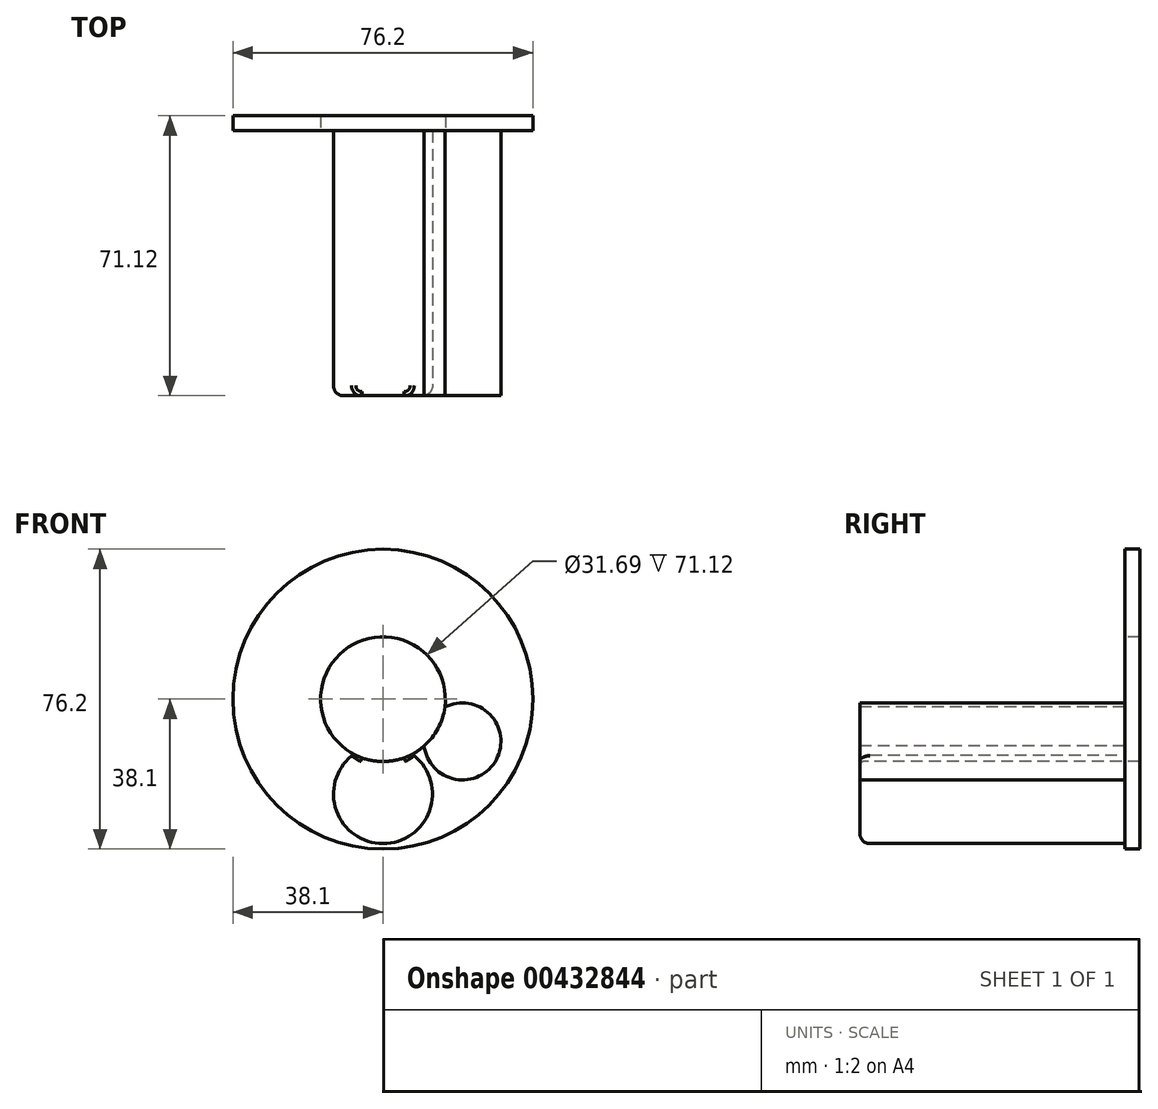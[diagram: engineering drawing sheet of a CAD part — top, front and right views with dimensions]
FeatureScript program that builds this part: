
annotation { "Feature Type Name" : "Feature", "Feature Type Description" : "" }
export const myFeature = defineFeature(function(context is Context, id is Id, definition is map)
    precondition{}
    {
        {
            var Q0;
            Q0=qCreatedBy(makeId("Front.planeOp"),FACE);
            var sketch = newSketch(context, id + "F0", { "sketchPlane" : qUnion([Q0])});
            skCircle(sketch, "E0", {"center": v(0, 0) * mm, "radius": 38.1 * mm});
            skSolve(sketch);
        }
        {
            var Q0;
            Q0=makeQuery(id+"F0.imprint","IMPRINT",FACE,{"disambiguationData":[TD([[makeQuery(id+"F0.imprint","IMPRINT",EDGE,{"derivedFrom":sQuery(id+"F0.wireOp",EDGE,"E0")}),1.0]])]});
            extrude(context, id + "F1", {"entities" : qUnion([Q0]), "depth" : 71.12 * mm});
        }
        {
            var Q0;
            Q0=makeQuery(id+"F1.opExtrude","CAP_FACE",FACE,{"disambiguationData":[OSD([sQuery(id+"F0.wireOp",EDGE,"E0")])],"isStart":false});
            var sketch = newSketch(context, id + "F2", { "sketchPlane" : qUnion([Q0])});
            skCircle(sketch, "E1", {"center": v(0, 24.13) * mm, "radius": 12.57 * mm});
            skCircle(sketch, "E2.MirrorC", {"center": v(0, -24.13) * mm, "radius": 12.57 * mm});
            skLineSegment(sketch, "E3", {"start": v(0, 0) * mm, "end": v(-44.2, 26.56) * mm});
            skCircle(sketch, "E4", {"center": v(-19.6, 11.77) * mm, "radius": 9.27 * mm});
            skCircle(sketch, "E5", {"center": v(20.18, 10.73) * mm, "radius": 9.78 * mm});
            skCircle(sketch, "E6.MirrorC", {"center": v(20.18, -10.73) * mm, "radius": 9.78 * mm});
            skCircle(sketch, "E7", {"center": v(-20.72, -9.66) * mm, "radius": 10.92 * mm});
            skLineSegment(sketch, "E8", {"start": v(0, 0) * mm, "end": v(-20.72, -9.66) * mm});
            skLineSegment(sketch, "E9", {"start": v(0, 0) * mm, "end": v(20.18, 10.73) * mm});
            skLineSegment(sketch, "E10", {"start": v(20.18, -10.73) * mm, "end": v(0, 0) * mm});
            skSolve(sketch);
        }
        {
            var Q0;
            {var subQ0=sQuery(id+"F2.wireOp",EDGE,"E4");var subQ1=sQuery(id+"F2.wireOp",EDGE,"E3");var subQ2=makeQuery(id+"F2.imprint","INTERSECT",VERTEX,{"disambiguationData":[OD(0.0)],"derivedFrom":[subQ1,subQ0]});Q0=makeQuery(id+"F2.imprint","IMPRINT",FACE,{"disambiguationData":[TD([[makeQuery(id+"F2.imprint","IMPRINT",EDGE,{"disambiguationData":[TD([[subQ2,1.0]])],"derivedFrom":subQ1}),-1.0]])]});}
            var Q1;
            {var subQ0=sQuery(id+"F2.wireOp",EDGE,"E4");var subQ1=sQuery(id+"F2.wireOp",EDGE,"E3");var subQ2=makeQuery(id+"F2.imprint","INTERSECT",VERTEX,{"disambiguationData":[OD(0.0)],"derivedFrom":[subQ1,subQ0]});Q1=makeQuery(id+"F2.imprint","IMPRINT",FACE,{"disambiguationData":[TD([[makeQuery(id+"F2.imprint","IMPRINT",EDGE,{"disambiguationData":[TD([[subQ2,1.0]])],"derivedFrom":subQ1}),1.0]])]});}
            var Q2;
            Q2=makeQuery(id+"F2.imprint","IMPRINT",FACE,{"disambiguationData":[TD([[makeQuery(id+"F2.imprint","IMPRINT",EDGE,{"derivedFrom":sQuery(id+"F2.wireOp",EDGE,"E1")}),1.0]])]});
            var Q3;
            Q3=makeQuery(id+"F2.imprint","IMPRINT",FACE,{"disambiguationData":[TD([[makeQuery(id+"F2.imprint","IMPRINT",EDGE,{"derivedFrom":sQuery(id+"F2.wireOp",EDGE,"E5")}),1.0]])]});
            var Q4;
            Q4=makeQuery(id+"F2.imprint","IMPRINT",FACE,{"disambiguationData":[TD([[makeQuery(id+"F2.imprint","IMPRINT",EDGE,{"derivedFrom":sQuery(id+"F2.wireOp",EDGE,"E6.MirrorC")}),-1.0]])]});
            var Q5;
            Q5=makeQuery(id+"F2.imprint","IMPRINT",FACE,{"disambiguationData":[TD([[makeQuery(id+"F2.imprint","IMPRINT",EDGE,{"derivedFrom":sQuery(id+"F2.wireOp",EDGE,"E2.MirrorC")}),-1.0]])]});
            var Q6;
            Q6=makeQuery(id+"F2.imprint","IMPRINT",FACE,{"disambiguationData":[TD([[makeQuery(id+"F2.imprint","IMPRINT",EDGE,{"derivedFrom":sQuery(id+"F2.wireOp",EDGE,"E7")}),1.0]])]});
            extrude(context, id + "F3", {"entities" : qUnion([Q0, Q1, Q2, Q3, Q4, Q5, Q6]), "operationType" : NewBodyOperationType.REMOVE, "oppositeDirection" : true, "depth" : 67.3 * mm});
        }
        {
            var Q0;
            Q0=makeQuery(id+"F1.opExtrude","CAP_FACE",FACE,{"disambiguationData":[OSD([sQuery(id+"F0.wireOp",EDGE,"E0")])],"isStart":false});
            var sketch = newSketch(context, id + "F4", { "sketchPlane" : qUnion([Q0])});
            skCircle(sketch, "E11", {"center": v(0, 0) * mm, "radius": 15.84 * mm});
            skSolve(sketch);
        }
        {
            var Q0;
            {var subQ0=sQuery(id+"F4.wireOp",EDGE,"E11");var subQ1=makeQuery(id+"F3.boolean.opBoolean","COPY",EDGE,{"derivedFrom":makeQuery(id+"F3.opExtrude","CAP_EDGE",EDGE,{"disambiguationData":[OSD([sQuery(id+"F2.wireOp",EDGE,"E1")])],"isStart":true})});var subQ2=makeQuery(id+"F4.imprint","INTERSECT",VERTEX,{"disambiguationData":[OD(0.0)],"derivedFrom":[subQ1,subQ0]});Q0=makeQuery(id+"F4.imprint","IMPRINT",FACE,{"disambiguationData":[TD([[makeQuery(id+"F4.imprint","IMPRINT",EDGE,{"disambiguationData":[TD([[subQ2,-1.0]])],"derivedFrom":subQ0}),1.0]])]});}
            var Q1;
            {var subQ0=sQuery(id+"F4.wireOp",EDGE,"E11");var subQ1=makeQuery(id+"F3.boolean.opBoolean","COPY",EDGE,{"derivedFrom":makeQuery(id+"F3.opExtrude","CAP_EDGE",EDGE,{"disambiguationData":[OSD([sQuery(id+"F2.wireOp",EDGE,"E1")])],"isStart":true})});var subQ2=makeQuery(id+"F4.imprint","INTERSECT",VERTEX,{"disambiguationData":[OD(0.0)],"derivedFrom":[subQ1,subQ0]});Q1=makeQuery(id+"F4.imprint","IMPRINT",FACE,{"disambiguationData":[TD([[makeQuery(id+"F4.imprint","IMPRINT",EDGE,{"disambiguationData":[TD([[subQ2,1.0]])],"derivedFrom":subQ0}),1.0]])]});}
            var Q2;
            {var subQ0=sQuery(id+"F4.wireOp",EDGE,"E11");var subQ1=makeQuery(id+"F3.boolean.opBoolean","COPY",EDGE,{"derivedFrom":makeQuery(id+"F3.opExtrude","CAP_EDGE",EDGE,{"disambiguationData":[OSD([sQuery(id+"F2.wireOp",EDGE,"E2.MirrorC")])],"isStart":true})});var subQ2=makeQuery(id+"F4.imprint","INTERSECT",VERTEX,{"disambiguationData":[OD(0.0)],"derivedFrom":[subQ1,subQ0]});Q2=makeQuery(id+"F4.imprint","IMPRINT",FACE,{"disambiguationData":[TD([[makeQuery(id+"F4.imprint","IMPRINT",EDGE,{"disambiguationData":[TD([[subQ2,-1.0]])],"derivedFrom":subQ0}),1.0]])]});}
            var Q3;
            {var subQ0=sQuery(id+"F4.wireOp",EDGE,"E11");var subQ1=makeQuery(id+"F3.boolean.opBoolean","COPY",EDGE,{"derivedFrom":makeQuery(id+"F3.opExtrude","CAP_EDGE",EDGE,{"disambiguationData":[OSD([sQuery(id+"F2.wireOp",EDGE,"E7")])],"isStart":true})});var subQ2=makeQuery(id+"F4.imprint","INTERSECT",VERTEX,{"disambiguationData":[OD(0.0)],"derivedFrom":[subQ1,subQ0]});Q3=makeQuery(id+"F4.imprint","IMPRINT",FACE,{"disambiguationData":[TD([[makeQuery(id+"F4.imprint","IMPRINT",EDGE,{"disambiguationData":[TD([[subQ2,-1.0]])],"derivedFrom":subQ0}),1.0]])]});}
            var Q4;
            {var subQ0=sQuery(id+"F4.wireOp",EDGE,"E11");var subQ1=makeQuery(id+"F3.boolean.opBoolean","COPY",EDGE,{"derivedFrom":makeQuery(id+"F3.opExtrude","CAP_EDGE",EDGE,{"disambiguationData":[OSD([sQuery(id+"F2.wireOp",EDGE,"E5")])],"isStart":true})});var subQ2=makeQuery(id+"F4.imprint","INTERSECT",VERTEX,{"disambiguationData":[OD(0.0)],"derivedFrom":[subQ1,subQ0]});Q4=makeQuery(id+"F4.imprint","IMPRINT",FACE,{"disambiguationData":[TD([[makeQuery(id+"F4.imprint","IMPRINT",EDGE,{"disambiguationData":[TD([[subQ2,1.0]])],"derivedFrom":subQ0}),1.0]])]});}
            var Q5;
            {var subQ0=sQuery(id+"F4.wireOp",EDGE,"E11");var subQ1=makeQuery(id+"F3.boolean.opBoolean","COPY",EDGE,{"derivedFrom":makeQuery(id+"F3.opExtrude","CAP_EDGE",EDGE,{"disambiguationData":[OSD([sQuery(id+"F2.wireOp",EDGE,"E6.MirrorC")])],"isStart":true})});var subQ2=makeQuery(id+"F4.imprint","INTERSECT",VERTEX,{"disambiguationData":[OD(0.0)],"derivedFrom":[subQ1,subQ0]});Q5=makeQuery(id+"F4.imprint","IMPRINT",FACE,{"disambiguationData":[TD([[makeQuery(id+"F4.imprint","IMPRINT",EDGE,{"disambiguationData":[TD([[subQ2,-1.0]])],"derivedFrom":subQ0}),1.0]])]});}
            var Q6;
            {var subQ0=sQuery(id+"F4.wireOp",EDGE,"E11");var subQ1=makeQuery(id+"F3.boolean.opBoolean","COPY",EDGE,{"derivedFrom":makeQuery(id+"F3.opExtrude","CAP_EDGE",EDGE,{"disambiguationData":[OSD([sQuery(id+"F2.wireOp",EDGE,"E4")])],"isStart":true})});var subQ2=makeQuery(id+"F4.imprint","INTERSECT",VERTEX,{"disambiguationData":[OD(0.0)],"derivedFrom":[subQ1,subQ0]});Q6=makeQuery(id+"F4.imprint","IMPRINT",FACE,{"disambiguationData":[TD([[makeQuery(id+"F4.imprint","IMPRINT",EDGE,{"disambiguationData":[TD([[subQ2,-1.0]])],"derivedFrom":subQ0}),1.0]])]});}
            extrude(context, id + "F5", {"entities" : qUnion([Q0, Q1, Q2, Q3, Q4, Q5, Q6]), "operationType" : NewBodyOperationType.REMOVE, "oppositeDirection" : true, "depth" : 85.1 * mm});
        }
        {
            var Q0;
            Q0=makeQuery(id+"F3.boolean.opBoolean","COPY",EDGE,{"derivedFrom":makeQuery(id+"F3.opExtrude","CAP_EDGE",EDGE,{"disambiguationData":[OSD([sQuery(id+"F2.wireOp",EDGE,"E4")])],"isStart":true})});
            var Q1;
            Q1=makeQuery(id+"F3.boolean.opBoolean","COPY",EDGE,{"derivedFrom":makeQuery(id+"F3.opExtrude","CAP_EDGE",EDGE,{"disambiguationData":[OSD([sQuery(id+"F2.wireOp",EDGE,"E1")])],"isStart":true})});
            var Q2;
            Q2=makeQuery(id+"F3.boolean.opBoolean","COPY",EDGE,{"derivedFrom":makeQuery(id+"F3.opExtrude","CAP_EDGE",EDGE,{"disambiguationData":[OSD([sQuery(id+"F2.wireOp",EDGE,"E7")])],"isStart":true})});
            var Q3;
            Q3=makeQuery(id+"F3.boolean.opBoolean","COPY",EDGE,{"derivedFrom":makeQuery(id+"F3.opExtrude","CAP_EDGE",EDGE,{"disambiguationData":[OSD([sQuery(id+"F2.wireOp",EDGE,"E2.MirrorC")])],"isStart":true})});
            var Q4;
            Q4=makeQuery(id+"F3.boolean.opBoolean","COPY",EDGE,{"derivedFrom":makeQuery(id+"F3.opExtrude","CAP_EDGE",EDGE,{"disambiguationData":[OSD([sQuery(id+"F2.wireOp",EDGE,"E6.MirrorC")])],"isStart":true})});
            var Q5;
            Q5=makeQuery(id+"F3.boolean.opBoolean","COPY",EDGE,{"derivedFrom":makeQuery(id+"F3.opExtrude","CAP_EDGE",EDGE,{"disambiguationData":[OSD([sQuery(id+"F2.wireOp",EDGE,"E5")])],"isStart":true})});
            var Q6;
            Q6=makeQuery(id+"F1.opExtrude","CAP_EDGE",EDGE,{"disambiguationData":[OSD([sQuery(id+"F0.wireOp",EDGE,"E0")])],"isStart":false});
            fillet(context, id + "F6", {"entities" : qUnion([Q0, Q1, Q2, Q3, Q4, Q5, Q6]), "radius" : 2.54 * mm, "tangentPropagation" : true, "allowEdgeOverflow" : false});
        }
        {
            var Q0;
            {var subQ0=sQuery(id+"F4.wireOp",EDGE,"E11");var subQ1=sQuery(id+"F2.wireOp",EDGE,"E1");var subQ2=makeQuery(id+"F3.boolean.opBoolean","COPY",EDGE,{"derivedFrom":makeQuery(id+"F3.opExtrude","CAP_EDGE",EDGE,{"disambiguationData":[OSD([subQ1])],"isStart":true})});var subQ3=makeQuery(id+"F4.imprint","INTERSECT",VERTEX,{"disambiguationData":[OD(1.0)],"derivedFrom":[subQ2,subQ0]});var subQ4=makeQuery(id+"F4.imprint","INTERSECT",VERTEX,{"disambiguationData":[OD(0.0)],"derivedFrom":[subQ2,subQ0]});Q0=makeQuery(id+"F5.boolean.opBoolean","INTERSECT",EDGE,{"disambiguationData":[OD(0.0)],"derivedFrom":[makeQuery(id+"F3.boolean.opBoolean","COPY",FACE,{"derivedFrom":makeQuery(id+"F3.opExtrude","SWEPT_FACE",FACE,{"disambiguationData":[OSD([subQ1])]})}),makeQuery(id+"F5.opExtrude","SWEPT_FACE",FACE,{"disambiguationData":[OSD([subQ0]),TDD([makeQuery(id+"F4.imprint","IMPRINT",EDGE,{"disambiguationData":[TD([[makeQuery(id+"F4.imprint","INTERSECT",VERTEX,{"disambiguationData":[OD(0.0)],"derivedFrom":[makeQuery(id+"F3.boolean.opBoolean","COPY",EDGE,{"derivedFrom":makeQuery(id+"F3.opExtrude","CAP_EDGE",EDGE,{"disambiguationData":[OSD([sQuery(id+"F2.wireOp",EDGE,"E5")])],"isStart":true})}),subQ0]}),-1.0]])],"derivedFrom":subQ0}),makeQuery(id+"F4.imprint","IMPRINT",EDGE,{"disambiguationData":[TD([[subQ4,-1.0]])],"derivedFrom":subQ0}),makeQuery(id+"F4.imprint","IMPRINT",EDGE,{"disambiguationData":[TD([[subQ3,-1.0]])],"derivedFrom":subQ0})])]})]});}
            var Q1;
            {var subQ0=sQuery(id+"F2.wireOp",EDGE,"E5");var subQ1=sQuery(id+"F4.wireOp",EDGE,"E11");var subQ5=makeQuery(id+"F4.imprint","INTERSECT",VERTEX,{"disambiguationData":[OD(0.0)],"derivedFrom":[makeQuery(id+"F3.boolean.opBoolean","COPY",EDGE,{"derivedFrom":makeQuery(id+"F3.opExtrude","CAP_EDGE",EDGE,{"disambiguationData":[OSD([subQ0])],"isStart":true})}),subQ1]});Q1=makeQuery(id+"F5.boolean.opBoolean","COPY",EDGE,{"disambiguationData":[topologyDisambiguationEdgeConnected([makeQuery(id+"F3.boolean.opBoolean","COPY",FACE,{"derivedFrom":makeQuery(id+"F3.opExtrude","SWEPT_FACE",FACE,{"disambiguationData":[OSD([subQ0])]})})])],"derivedFrom":makeQuery(id+"F5.opExtrude","SWEPT_EDGE",EDGE,{"disambiguationData":[OSD([subQ0,subQ1]),TDD([subQ5])]})});}
            var Q2;
            {var subQ0=sQuery(id+"F4.wireOp",EDGE,"E11");var subQ1=sQuery(id+"F2.wireOp",EDGE,"E1");var subQ2=makeQuery(id+"F3.boolean.opBoolean","COPY",EDGE,{"derivedFrom":makeQuery(id+"F3.opExtrude","CAP_EDGE",EDGE,{"disambiguationData":[OSD([subQ1])],"isStart":true})});var subQ3=makeQuery(id+"F4.imprint","INTERSECT",VERTEX,{"disambiguationData":[OD(1.0)],"derivedFrom":[subQ2,subQ0]});var subQ4=makeQuery(id+"F4.imprint","INTERSECT",VERTEX,{"disambiguationData":[OD(0.0)],"derivedFrom":[subQ2,subQ0]});Q2=makeQuery(id+"F5.boolean.opBoolean","INTERSECT",EDGE,{"disambiguationData":[OD(1.0)],"derivedFrom":[makeQuery(id+"F3.boolean.opBoolean","COPY",FACE,{"derivedFrom":makeQuery(id+"F3.opExtrude","SWEPT_FACE",FACE,{"disambiguationData":[OSD([subQ1])]})}),makeQuery(id+"F5.opExtrude","SWEPT_FACE",FACE,{"disambiguationData":[OSD([subQ0]),TDD([makeQuery(id+"F4.imprint","IMPRINT",EDGE,{"disambiguationData":[TD([[makeQuery(id+"F4.imprint","INTERSECT",VERTEX,{"disambiguationData":[OD(0.0)],"derivedFrom":[makeQuery(id+"F3.boolean.opBoolean","COPY",EDGE,{"derivedFrom":makeQuery(id+"F3.opExtrude","CAP_EDGE",EDGE,{"disambiguationData":[OSD([sQuery(id+"F2.wireOp",EDGE,"E5")])],"isStart":true})}),subQ0]}),-1.0]])],"derivedFrom":subQ0}),makeQuery(id+"F4.imprint","IMPRINT",EDGE,{"disambiguationData":[TD([[subQ4,-1.0]])],"derivedFrom":subQ0}),makeQuery(id+"F4.imprint","IMPRINT",EDGE,{"disambiguationData":[TD([[subQ3,-1.0]])],"derivedFrom":subQ0})])]})]});}
            var Q3;
            {var subQ0=sQuery(id+"F2.wireOp",EDGE,"E5");var subQ1=sQuery(id+"F4.wireOp",EDGE,"E11");var subQ2=makeQuery(id+"F4.imprint","INTERSECT",VERTEX,{"disambiguationData":[OD(1.0)],"derivedFrom":[makeQuery(id+"F3.boolean.opBoolean","COPY",EDGE,{"derivedFrom":makeQuery(id+"F3.opExtrude","CAP_EDGE",EDGE,{"disambiguationData":[OSD([subQ0])],"isStart":true})}),subQ1]});Q3=makeQuery(id+"F5.boolean.opBoolean","COPY",EDGE,{"disambiguationData":[topologyDisambiguationEdgeConnected([makeQuery(id+"F3.boolean.opBoolean","COPY",FACE,{"derivedFrom":makeQuery(id+"F3.opExtrude","SWEPT_FACE",FACE,{"disambiguationData":[OSD([subQ0])]})})])],"derivedFrom":makeQuery(id+"F5.opExtrude","SWEPT_EDGE",EDGE,{"disambiguationData":[OSD([subQ0,subQ1]),TDD([subQ2])]})});}
            var Q4;
            {var subQ0=sQuery(id+"F2.wireOp",EDGE,"E6.MirrorC");var subQ1=sQuery(id+"F4.wireOp",EDGE,"E11");var subQ2=makeQuery(id+"F4.imprint","INTERSECT",VERTEX,{"disambiguationData":[OD(1.0)],"derivedFrom":[makeQuery(id+"F3.boolean.opBoolean","COPY",EDGE,{"derivedFrom":makeQuery(id+"F3.opExtrude","CAP_EDGE",EDGE,{"disambiguationData":[OSD([subQ0])],"isStart":true})}),subQ1]});Q4=makeQuery(id+"F5.boolean.opBoolean","COPY",EDGE,{"disambiguationData":[topologyDisambiguationEdgeConnected([makeQuery(id+"F3.boolean.opBoolean","COPY",FACE,{"derivedFrom":makeQuery(id+"F3.opExtrude","SWEPT_FACE",FACE,{"disambiguationData":[OSD([subQ0])]})})])],"derivedFrom":makeQuery(id+"F5.opExtrude","SWEPT_EDGE",EDGE,{"disambiguationData":[OSD([subQ0,subQ1]),TDD([subQ2])]})});}
            var Q5;
            {var subQ0=sQuery(id+"F2.wireOp",EDGE,"E6.MirrorC");var subQ1=sQuery(id+"F4.wireOp",EDGE,"E11");var subQ4=makeQuery(id+"F4.imprint","INTERSECT",VERTEX,{"disambiguationData":[OD(0.0)],"derivedFrom":[makeQuery(id+"F3.boolean.opBoolean","COPY",EDGE,{"derivedFrom":makeQuery(id+"F3.opExtrude","CAP_EDGE",EDGE,{"disambiguationData":[OSD([subQ0])],"isStart":true})}),subQ1]});Q5=makeQuery(id+"F5.boolean.opBoolean","COPY",EDGE,{"disambiguationData":[topologyDisambiguationEdgeConnected([makeQuery(id+"F3.boolean.opBoolean","COPY",FACE,{"derivedFrom":makeQuery(id+"F3.opExtrude","SWEPT_FACE",FACE,{"disambiguationData":[OSD([subQ0])]})})])],"derivedFrom":makeQuery(id+"F5.opExtrude","SWEPT_EDGE",EDGE,{"disambiguationData":[OSD([subQ0,subQ1]),TDD([subQ4])]})});}
            var Q6;
            {var subQ0=sQuery(id+"F4.wireOp",EDGE,"E11");var subQ1=sQuery(id+"F2.wireOp",EDGE,"E2.MirrorC");var subQ2=makeQuery(id+"F3.boolean.opBoolean","COPY",EDGE,{"derivedFrom":makeQuery(id+"F3.opExtrude","CAP_EDGE",EDGE,{"disambiguationData":[OSD([subQ1])],"isStart":true})});var subQ3=makeQuery(id+"F4.imprint","INTERSECT",VERTEX,{"disambiguationData":[OD(1.0)],"derivedFrom":[subQ2,subQ0]});var subQ4=makeQuery(id+"F4.imprint","INTERSECT",VERTEX,{"disambiguationData":[OD(0.0)],"derivedFrom":[subQ2,subQ0]});var subQ5=makeQuery(id+"F3.boolean.opBoolean","COPY",EDGE,{"derivedFrom":makeQuery(id+"F3.opExtrude","CAP_EDGE",EDGE,{"disambiguationData":[OSD([sQuery(id+"F2.wireOp",EDGE,"E7")])],"isStart":true})});var subQ6=makeQuery(id+"F4.imprint","INTERSECT",VERTEX,{"disambiguationData":[OD(1.0)],"derivedFrom":[subQ5,subQ0]});var subQ7=makeQuery(id+"F4.imprint","INTERSECT",VERTEX,{"disambiguationData":[OD(0.0)],"derivedFrom":[subQ5,subQ0]});Q6=makeQuery(id+"F5.boolean.opBoolean","INTERSECT",EDGE,{"disambiguationData":[OD(0.0)],"derivedFrom":[makeQuery(id+"F3.boolean.opBoolean","COPY",FACE,{"derivedFrom":makeQuery(id+"F3.opExtrude","SWEPT_FACE",FACE,{"disambiguationData":[OSD([subQ1])]})}),makeQuery(id+"F5.opExtrude","SWEPT_FACE",FACE,{"disambiguationData":[OSD([subQ0]),TDD([makeQuery(id+"F4.imprint","IMPRINT",EDGE,{"disambiguationData":[TD([[makeQuery(id+"F4.imprint","INTERSECT",VERTEX,{"disambiguationData":[OD(1.0)],"derivedFrom":[makeQuery(id+"F3.boolean.opBoolean","COPY",EDGE,{"derivedFrom":makeQuery(id+"F3.opExtrude","CAP_EDGE",EDGE,{"disambiguationData":[OSD([sQuery(id+"F2.wireOp",EDGE,"E4")])],"isStart":true})}),subQ0]}),-1.0]])],"derivedFrom":subQ0}),makeQuery(id+"F4.imprint","IMPRINT",EDGE,{"disambiguationData":[TD([[subQ7,-1.0]])],"derivedFrom":subQ0}),makeQuery(id+"F4.imprint","IMPRINT",EDGE,{"disambiguationData":[TD([[subQ6,-1.0]])],"derivedFrom":subQ0}),makeQuery(id+"F4.imprint","IMPRINT",EDGE,{"disambiguationData":[TD([[subQ4,-1.0]])],"derivedFrom":subQ0}),makeQuery(id+"F4.imprint","IMPRINT",EDGE,{"disambiguationData":[TD([[subQ3,-1.0]])],"derivedFrom":subQ0})])]})]});}
            var Q7;
            {var subQ0=sQuery(id+"F4.wireOp",EDGE,"E11");var subQ1=sQuery(id+"F2.wireOp",EDGE,"E2.MirrorC");var subQ2=makeQuery(id+"F3.boolean.opBoolean","COPY",EDGE,{"derivedFrom":makeQuery(id+"F3.opExtrude","CAP_EDGE",EDGE,{"disambiguationData":[OSD([subQ1])],"isStart":true})});var subQ3=makeQuery(id+"F4.imprint","INTERSECT",VERTEX,{"disambiguationData":[OD(1.0)],"derivedFrom":[subQ2,subQ0]});var subQ4=makeQuery(id+"F4.imprint","INTERSECT",VERTEX,{"disambiguationData":[OD(0.0)],"derivedFrom":[subQ2,subQ0]});var subQ5=makeQuery(id+"F3.boolean.opBoolean","COPY",EDGE,{"derivedFrom":makeQuery(id+"F3.opExtrude","CAP_EDGE",EDGE,{"disambiguationData":[OSD([sQuery(id+"F2.wireOp",EDGE,"E7")])],"isStart":true})});var subQ6=makeQuery(id+"F4.imprint","INTERSECT",VERTEX,{"disambiguationData":[OD(1.0)],"derivedFrom":[subQ5,subQ0]});var subQ7=makeQuery(id+"F4.imprint","INTERSECT",VERTEX,{"disambiguationData":[OD(0.0)],"derivedFrom":[subQ5,subQ0]});Q7=makeQuery(id+"F5.boolean.opBoolean","INTERSECT",EDGE,{"disambiguationData":[OD(1.0)],"derivedFrom":[makeQuery(id+"F3.boolean.opBoolean","COPY",FACE,{"derivedFrom":makeQuery(id+"F3.opExtrude","SWEPT_FACE",FACE,{"disambiguationData":[OSD([subQ1])]})}),makeQuery(id+"F5.opExtrude","SWEPT_FACE",FACE,{"disambiguationData":[OSD([subQ0]),TDD([makeQuery(id+"F4.imprint","IMPRINT",EDGE,{"disambiguationData":[TD([[makeQuery(id+"F4.imprint","INTERSECT",VERTEX,{"disambiguationData":[OD(1.0)],"derivedFrom":[makeQuery(id+"F3.boolean.opBoolean","COPY",EDGE,{"derivedFrom":makeQuery(id+"F3.opExtrude","CAP_EDGE",EDGE,{"disambiguationData":[OSD([sQuery(id+"F2.wireOp",EDGE,"E4")])],"isStart":true})}),subQ0]}),-1.0]])],"derivedFrom":subQ0}),makeQuery(id+"F4.imprint","IMPRINT",EDGE,{"disambiguationData":[TD([[subQ7,-1.0]])],"derivedFrom":subQ0}),makeQuery(id+"F4.imprint","IMPRINT",EDGE,{"disambiguationData":[TD([[subQ6,-1.0]])],"derivedFrom":subQ0}),makeQuery(id+"F4.imprint","IMPRINT",EDGE,{"disambiguationData":[TD([[subQ4,-1.0]])],"derivedFrom":subQ0}),makeQuery(id+"F4.imprint","IMPRINT",EDGE,{"disambiguationData":[TD([[subQ3,-1.0]])],"derivedFrom":subQ0})])]})]});}
            var Q8;
            {var subQ0=sQuery(id+"F2.wireOp",EDGE,"E4");var subQ1=sQuery(id+"F4.wireOp",EDGE,"E11");var subQ8=makeQuery(id+"F4.imprint","INTERSECT",VERTEX,{"disambiguationData":[OD(1.0)],"derivedFrom":[makeQuery(id+"F3.boolean.opBoolean","COPY",EDGE,{"derivedFrom":makeQuery(id+"F3.opExtrude","CAP_EDGE",EDGE,{"disambiguationData":[OSD([subQ0])],"isStart":true})}),subQ1]});Q8=makeQuery(id+"F5.boolean.opBoolean","COPY",EDGE,{"disambiguationData":[topologyDisambiguationEdgeConnected([makeQuery(id+"F3.boolean.opBoolean","COPY",FACE,{"derivedFrom":makeQuery(id+"F3.opExtrude","SWEPT_FACE",FACE,{"disambiguationData":[OSD([subQ0])]})})])],"derivedFrom":makeQuery(id+"F5.opExtrude","SWEPT_EDGE",EDGE,{"disambiguationData":[OSD([subQ0,subQ1]),TDD([subQ8])]})});}
            var Q9;
            {var subQ0=sQuery(id+"F4.wireOp",EDGE,"E11");var subQ1=makeQuery(id+"F3.boolean.opBoolean","COPY",EDGE,{"derivedFrom":makeQuery(id+"F3.opExtrude","CAP_EDGE",EDGE,{"disambiguationData":[OSD([sQuery(id+"F2.wireOp",EDGE,"E2.MirrorC")])],"isStart":true})});var subQ2=makeQuery(id+"F4.imprint","INTERSECT",VERTEX,{"disambiguationData":[OD(1.0)],"derivedFrom":[subQ1,subQ0]});var subQ3=makeQuery(id+"F4.imprint","INTERSECT",VERTEX,{"disambiguationData":[OD(0.0)],"derivedFrom":[subQ1,subQ0]});var subQ4=sQuery(id+"F2.wireOp",EDGE,"E7");var subQ5=makeQuery(id+"F3.boolean.opBoolean","COPY",EDGE,{"derivedFrom":makeQuery(id+"F3.opExtrude","CAP_EDGE",EDGE,{"disambiguationData":[OSD([subQ4])],"isStart":true})});var subQ6=makeQuery(id+"F4.imprint","INTERSECT",VERTEX,{"disambiguationData":[OD(1.0)],"derivedFrom":[subQ5,subQ0]});var subQ7=makeQuery(id+"F4.imprint","INTERSECT",VERTEX,{"disambiguationData":[OD(0.0)],"derivedFrom":[subQ5,subQ0]});Q9=makeQuery(id+"F5.boolean.opBoolean","INTERSECT",EDGE,{"disambiguationData":[OD(0.0)],"derivedFrom":[makeQuery(id+"F3.boolean.opBoolean","COPY",FACE,{"derivedFrom":makeQuery(id+"F3.opExtrude","SWEPT_FACE",FACE,{"disambiguationData":[OSD([subQ4])]})}),makeQuery(id+"F5.opExtrude","SWEPT_FACE",FACE,{"disambiguationData":[OSD([subQ0]),TDD([makeQuery(id+"F4.imprint","IMPRINT",EDGE,{"disambiguationData":[TD([[makeQuery(id+"F4.imprint","INTERSECT",VERTEX,{"disambiguationData":[OD(1.0)],"derivedFrom":[makeQuery(id+"F3.boolean.opBoolean","COPY",EDGE,{"derivedFrom":makeQuery(id+"F3.opExtrude","CAP_EDGE",EDGE,{"disambiguationData":[OSD([sQuery(id+"F2.wireOp",EDGE,"E4")])],"isStart":true})}),subQ0]}),-1.0]])],"derivedFrom":subQ0}),makeQuery(id+"F4.imprint","IMPRINT",EDGE,{"disambiguationData":[TD([[subQ7,-1.0]])],"derivedFrom":subQ0}),makeQuery(id+"F4.imprint","IMPRINT",EDGE,{"disambiguationData":[TD([[subQ6,-1.0]])],"derivedFrom":subQ0}),makeQuery(id+"F4.imprint","IMPRINT",EDGE,{"disambiguationData":[TD([[subQ3,-1.0]])],"derivedFrom":subQ0}),makeQuery(id+"F4.imprint","IMPRINT",EDGE,{"disambiguationData":[TD([[subQ2,-1.0]])],"derivedFrom":subQ0})])]})]});}
            var Q10;
            {var subQ0=sQuery(id+"F2.wireOp",EDGE,"E4");var subQ1=sQuery(id+"F4.wireOp",EDGE,"E11");var subQ4=makeQuery(id+"F4.imprint","INTERSECT",VERTEX,{"disambiguationData":[OD(0.0)],"derivedFrom":[makeQuery(id+"F3.boolean.opBoolean","COPY",EDGE,{"derivedFrom":makeQuery(id+"F3.opExtrude","CAP_EDGE",EDGE,{"disambiguationData":[OSD([subQ0])],"isStart":true})}),subQ1]});Q10=makeQuery(id+"F5.boolean.opBoolean","COPY",EDGE,{"disambiguationData":[topologyDisambiguationEdgeConnected([makeQuery(id+"F3.boolean.opBoolean","COPY",FACE,{"derivedFrom":makeQuery(id+"F3.opExtrude","SWEPT_FACE",FACE,{"disambiguationData":[OSD([subQ0])]})})])],"derivedFrom":makeQuery(id+"F5.opExtrude","SWEPT_EDGE",EDGE,{"disambiguationData":[OSD([subQ0,subQ1]),TDD([subQ4])]})});}
            var Q11;
            {var subQ0=sQuery(id+"F4.wireOp",EDGE,"E11");var subQ1=makeQuery(id+"F3.boolean.opBoolean","COPY",EDGE,{"derivedFrom":makeQuery(id+"F3.opExtrude","CAP_EDGE",EDGE,{"disambiguationData":[OSD([sQuery(id+"F2.wireOp",EDGE,"E2.MirrorC")])],"isStart":true})});var subQ2=makeQuery(id+"F4.imprint","INTERSECT",VERTEX,{"disambiguationData":[OD(1.0)],"derivedFrom":[subQ1,subQ0]});var subQ3=makeQuery(id+"F4.imprint","INTERSECT",VERTEX,{"disambiguationData":[OD(0.0)],"derivedFrom":[subQ1,subQ0]});var subQ4=sQuery(id+"F2.wireOp",EDGE,"E7");var subQ5=makeQuery(id+"F3.boolean.opBoolean","COPY",EDGE,{"derivedFrom":makeQuery(id+"F3.opExtrude","CAP_EDGE",EDGE,{"disambiguationData":[OSD([subQ4])],"isStart":true})});var subQ6=makeQuery(id+"F4.imprint","INTERSECT",VERTEX,{"disambiguationData":[OD(1.0)],"derivedFrom":[subQ5,subQ0]});var subQ7=makeQuery(id+"F4.imprint","INTERSECT",VERTEX,{"disambiguationData":[OD(0.0)],"derivedFrom":[subQ5,subQ0]});Q11=makeQuery(id+"F5.boolean.opBoolean","INTERSECT",EDGE,{"disambiguationData":[OD(1.0)],"derivedFrom":[makeQuery(id+"F3.boolean.opBoolean","COPY",FACE,{"derivedFrom":makeQuery(id+"F3.opExtrude","SWEPT_FACE",FACE,{"disambiguationData":[OSD([subQ4])]})}),makeQuery(id+"F5.opExtrude","SWEPT_FACE",FACE,{"disambiguationData":[OSD([subQ0]),TDD([makeQuery(id+"F4.imprint","IMPRINT",EDGE,{"disambiguationData":[TD([[makeQuery(id+"F4.imprint","INTERSECT",VERTEX,{"disambiguationData":[OD(1.0)],"derivedFrom":[makeQuery(id+"F3.boolean.opBoolean","COPY",EDGE,{"derivedFrom":makeQuery(id+"F3.opExtrude","CAP_EDGE",EDGE,{"disambiguationData":[OSD([sQuery(id+"F2.wireOp",EDGE,"E4")])],"isStart":true})}),subQ0]}),-1.0]])],"derivedFrom":subQ0}),makeQuery(id+"F4.imprint","IMPRINT",EDGE,{"disambiguationData":[TD([[subQ7,-1.0]])],"derivedFrom":subQ0}),makeQuery(id+"F4.imprint","IMPRINT",EDGE,{"disambiguationData":[TD([[subQ6,-1.0]])],"derivedFrom":subQ0}),makeQuery(id+"F4.imprint","IMPRINT",EDGE,{"disambiguationData":[TD([[subQ3,-1.0]])],"derivedFrom":subQ0}),makeQuery(id+"F4.imprint","IMPRINT",EDGE,{"disambiguationData":[TD([[subQ2,-1.0]])],"derivedFrom":subQ0})])]})]});}
            fillet(context, id + "F7", {"entities" : qUnion([Q0, Q1, Q2, Q3, Q4, Q5, Q6, Q7, Q8, Q9, Q10, Q11]), "radius" : 1.02 * mm, "tangentPropagation" : true, "allowEdgeOverflow" : false});
        }
    });
